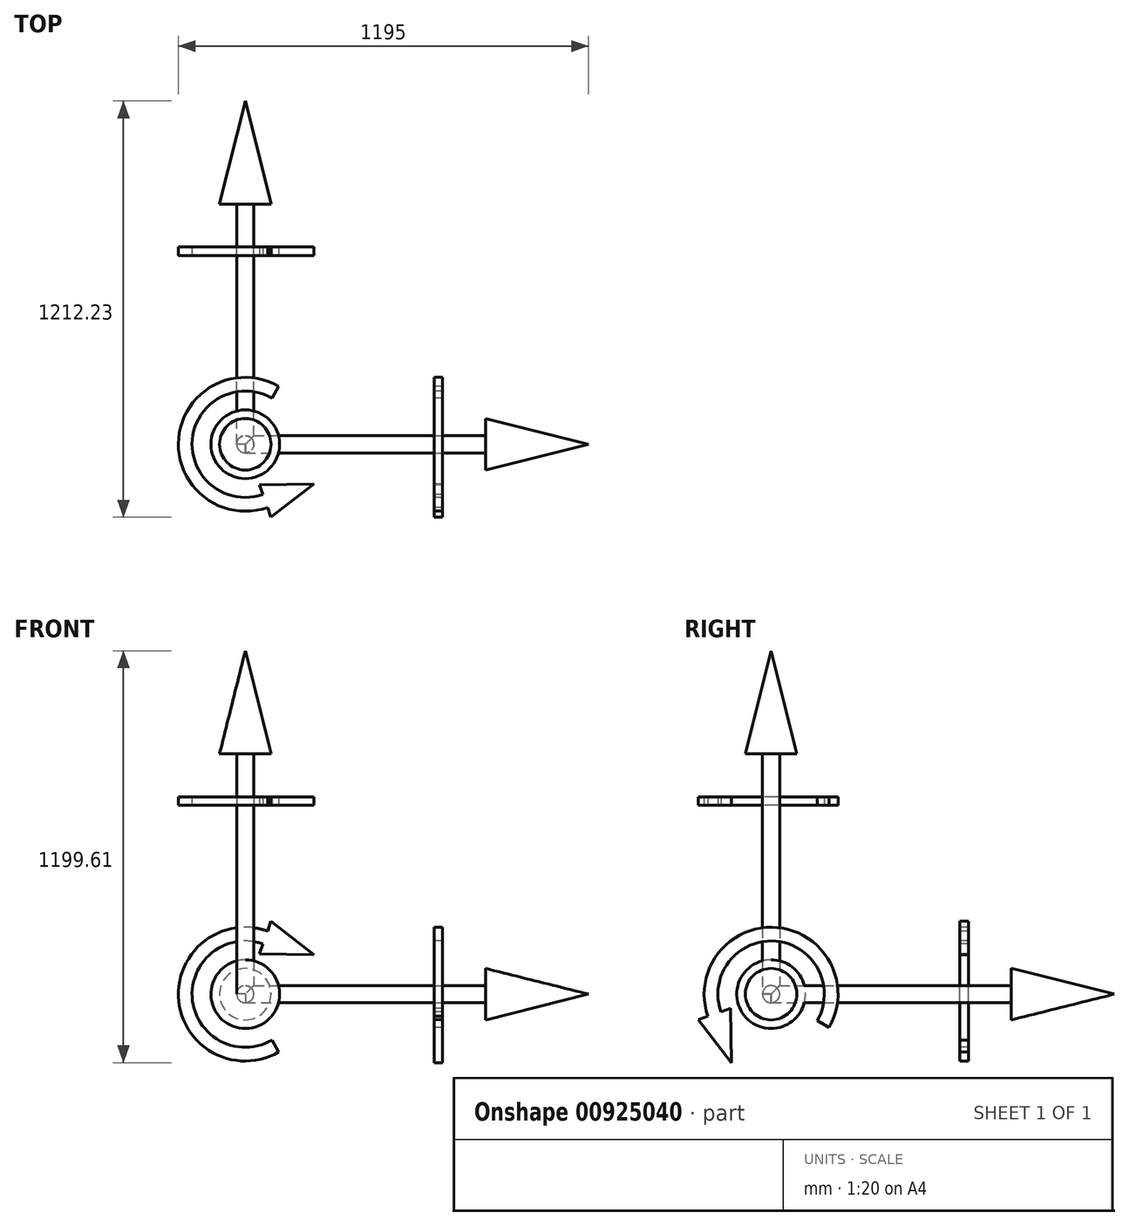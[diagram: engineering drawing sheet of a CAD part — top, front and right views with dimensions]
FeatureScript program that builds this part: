
annotation { "Feature Type Name" : "Feature", "Feature Type Description" : "" }
export const myFeature = defineFeature(function(context is Context, id is Id, definition is map)
    precondition{}
    {
        {
            var Q0;
            Q0=qCreatedBy(makeId("Front.planeOp"),FACE);
            var sketch = newSketch(context, id + "F0", { "sketchPlane" : qUnion([Q0])});
            skLineSegment(sketch, "E0.bottom", {"start": v(700, 0) * mm, "end": v(0, 0) * mm});
            skLineSegment(sketch, "E0.top", {"start": v(700, 25) * mm, "end": v(0, 25) * mm});
            skLineSegment(sketch, "E0.left", {"start": v(0, 0) * mm, "end": v(0, 25) * mm});
            skLineSegment(sketch, "E0.right", {"start": v(700, 0) * mm, "end": v(700, 25) * mm});
            skLineSegment(sketch, "E1", {"start": v(0, 0) * mm, "end": v(-428.97, 0) * mm, "construction": true});
            skLineSegment(sketch, "E2", {"start": v(700, 75) * mm, "end": v(1000, 0) * mm});
            skLineSegment(sketch, "E3", {"start": v(700, 0) * mm, "end": v(1000, 0) * mm});
            skLineSegment(sketch, "E4", {"start": v(700, 25) * mm, "end": v(700, 75) * mm});
            skSolve(sketch);
        }
        {
            var Q0;
            Q0=makeQuery(id+"F0.imprint","IMPRINT",FACE,{"disambiguationData":[TD([[makeQuery(id+"F0.imprint","IMPRINT",EDGE,{"derivedFrom":sQuery(id+"F0.wireOp",EDGE,"E0.right")}),-1.0]])]});
            var Q1;
            Q1=makeQuery(id+"F0.imprint","IMPRINT",FACE,{"disambiguationData":[TD([[makeQuery(id+"F0.imprint","IMPRINT",EDGE,{"derivedFrom":sQuery(id+"F0.wireOp",EDGE,"E0.bottom")}),-1.0]])]});
            var Q2;
            Q2=sQuery(id+"F0.wireOp",EDGE,"E0.bottom");
            revolve(context, id + "F1", {"surfaceOperationType" : NewSurfaceOperationType.NEW, "entities" : qUnion([Q0, Q1]), "axis" : qUnion([Q2]), "revolveType" : RevolveType.FULL});
        }
        {
            var Q0;
            Q0=qCreatedBy(makeId("Right.planeOp"),FACE);
            var sketch = newSketch(context, id + "F2", { "sketchPlane" : qUnion([Q0])});
            skLineSegment(sketch, "E5", {"start": v(1000, 0) * mm, "end": v(0, 0) * mm});
            skLineSegment(sketch, "E6", {"start": v(1000, 0) * mm, "end": v(700, 75) * mm});
            skLineSegment(sketch, "E7", {"start": v(700, 75) * mm, "end": v(700, 25) * mm});
            skLineSegment(sketch, "E8", {"start": v(0, 25) * mm, "end": v(700, 25) * mm});
            skLineSegment(sketch, "E9", {"start": v(0, 25) * mm, "end": v(0, 0) * mm});
            skSolve(sketch);
        }
        {
            var Q0;
            Q0=makeQuery(id+"F2.imprint","IMPRINT",FACE,{"disambiguationData":[TD([[makeQuery(id+"F2.imprint","IMPRINT",EDGE,{"derivedFrom":sQuery(id+"F2.wireOp",EDGE,"E5")}),-1.0]])]});
            var Q1;
            Q1=sQuery(id+"F2.wireOp",EDGE,"E5");
            revolve(context, id + "F3", {"operationType" : NewBodyOperationType.ADD, "surfaceOperationType" : NewSurfaceOperationType.NEW, "entities" : qUnion([Q0]), "axis" : qUnion([Q1]), "revolveType" : RevolveType.FULL});
        }
        {
            var Q0;
            Q0=qCreatedBy(makeId("Front.planeOp"),FACE);
            var sketch = newSketch(context, id + "F4", { "sketchPlane" : qUnion([Q0])});
            skLineSegment(sketch, "E10", {"start": v(0, 0) * mm, "end": v(0, 1000) * mm});
            skLineSegment(sketch, "E11", {"start": v(0, 1000) * mm, "end": v(-75, 700) * mm});
            skLineSegment(sketch, "E12", {"start": v(-75, 700) * mm, "end": v(-25, 700) * mm});
            skLineSegment(sketch, "E13", {"start": v(-25, 700) * mm, "end": v(-25, 0) * mm});
            skLineSegment(sketch, "E14", {"start": v(-25, 0) * mm, "end": v(0, 0) * mm});
            skSolve(sketch);
        }
        {
            var Q0;
            Q0=makeQuery(id+"F4.imprint","IMPRINT",FACE,{"disambiguationData":[TD([[makeQuery(id+"F4.imprint","IMPRINT",EDGE,{"derivedFrom":sQuery(id+"F4.wireOp",EDGE,"E10")}),1.0]])]});
            var Q1;
            Q1=sQuery(id+"F4.wireOp",EDGE,"E10");
            revolve(context, id + "F5", {"operationType" : NewBodyOperationType.ADD, "surfaceOperationType" : NewSurfaceOperationType.NEW, "entities" : qUnion([Q0]), "axis" : qUnion([Q1]), "revolveType" : RevolveType.FULL});
        }
        {
            var Q0;
            Q0=qCreatedBy(makeId("Right.planeOp"),FACE);
            var sketch = newSketch(context, id + "F6", { "sketchPlane" : qUnion([Q0])});
            skArc(sketch, "E15", {"start": v(0, -100) * mm, "mid": v(100, 0) * mm, "end": v(0, 100) * mm});
            skLineSegment(sketch, "E16", {"start": v(0, 100) * mm, "end": v(0, -100) * mm});
            skSolve(sketch);
        }
        {
            var Q0;
            Q0=makeQuery(id+"F6.imprint","IMPRINT",FACE,{"disambiguationData":[TD([[makeQuery(id+"F6.imprint","IMPRINT",EDGE,{"derivedFrom":sQuery(id+"F6.wireOp",EDGE,"E15")}),1.0]])]});
            var Q1;
            Q1=sQuery(id+"F6.wireOp",EDGE,"E16");
            revolve(context, id + "F7", {"surfaceOperationType" : NewSurfaceOperationType.NEW, "entities" : qUnion([Q0]), "axis" : qUnion([Q1]), "revolveType" : RevolveType.FULL});
        }
        {
            var Q0;
            Q0=qCreatedBy(makeId("Top.planeOp"),FACE);
            cPlane(context, id + "F8", {"entities" : qUnion([Q0]), "cplaneType" : CPlaneType.OFFSET, "offset" : 550 * mm, "width" : 150 * mm, "height" : 150 * mm});
        }
        {
            var Q0;
            Q0=qCreatedBy(id+"F8.planeOp",FACE);
            var sketch = newSketch(context, id + "F9", { "sketchPlane" : qUnion([Q0])});
            skArc(sketch, "E17", {"start": v(87.5, 151.55) * mm, "mid": v(-169.04, -45.3) * mm, "end": v(151.55, -87.5) * mm, "construction": true});
            skLineSegment(sketch, "E18", {"start": v(0, 0) * mm, "end": v(151.55, -87.5) * mm, "construction": true});
            skLineSegment(sketch, "E19", {"start": v(0, 0) * mm, "end": v(87.5, 151.55) * mm, "construction": true});
            skLineSegment(sketch, "E20", {"start": v(0, 0) * mm, "end": v(0, 998.9) * mm, "construction": true});
            skArc(sketch, "E21.0", {"start": v(97.5, 168.87) * mm, "mid": v(-194.17, 18.01) * mm, "end": v(64.77, -183.93) * mm});
            skArc(sketch, "E22.0", {"start": v(77.5, 134.23) * mm, "mid": v(-154.34, 14.32) * mm, "end": v(51.48, -146.2) * mm});
            skLineSegment(sketch, "E23", {"start": v(77.5, 134.23) * mm, "end": v(97.5, 168.87) * mm});
            skLineSegment(sketch, "E24", {"start": v(0, 0) * mm, "end": v(64.77, -183.93) * mm, "construction": true});
            skLineSegment(sketch, "E25", {"start": v(41.52, -117.9) * mm, "end": v(74.73, -212.23) * mm});
            skPoint(sketch, "E26", {"position": v(58.12, -165.07) * mm});
            skLineSegment(sketch, "E27", {"start": v(41.52, -117.9) * mm, "end": v(199.6, -115.24) * mm});
            skLineSegment(sketch, "E28", {"start": v(199.6, -115.24) * mm, "end": v(74.73, -212.23) * mm});
            skLineSegment(sketch, "E29", {"start": v(58.12, -165.07) * mm, "end": v(199.6, -115.24) * mm, "construction": true});
            skSolve(sketch);
        }
        {
            var Q0;
            {var subQ0=sQuery(id+"F9.wireOp",EDGE,"E21.0");Q0=makeQuery(id+"F9.imprint","IMPRINT",FACE,{"disambiguationData":[TD([[makeQuery(id+"F9.imprint","IMPRINT",EDGE,{"derivedFrom":subQ0}),1.0]])]});}
            var Q1;
            {var subQ0=sQuery(id+"F9.wireOp",EDGE,"E27");Q1=makeQuery(id+"F9.imprint","IMPRINT",FACE,{"disambiguationData":[TD([[makeQuery(id+"F9.imprint","IMPRINT",EDGE,{"derivedFrom":subQ0}),-1.0]])]});}
            extrude(context, id + "F10", {"entities" : qUnion([Q0, Q1]), "depth" : 25 * mm, "offsetDistance" : 25 * mm});
        }
        {
            var Q0;
            Q0=makeQuery(id+"F10.opExtrude","SWEPT_BODY",BODY,{"disambiguationData":[OSD([sQuery(id+"F9.wireOp",EDGE,"E21.0"),sQuery(id+"F9.wireOp",EDGE,"E22.0"),sQuery(id+"F9.wireOp",EDGE,"E23"),sQuery(id+"F9.wireOp",EDGE,"E25"),sQuery(id+"F9.wireOp",EDGE,"E27"),sQuery(id+"F9.wireOp",EDGE,"E28")])]});
            var Q1;
            Q1=makeQuery(id+"F3.opRevolve","SWEPT_FACE",FACE,{"disambiguationData":[OSD([sQuery(id+"F2.wireOp",EDGE,"E8")])]});
            transform(context, id + "F11", {"entities" : qUnion([Q0]), "transformType" : TransformType.ROTATION, "transformAxis" : qUnion([Q1]), "angle" : 90 * degree, "makeCopy" : true});
        }
        {
            var Q0;
            Q0=makeQuery(id+"F10.opExtrude","SWEPT_BODY",BODY,{"disambiguationData":[OSD([sQuery(id+"F9.wireOp",EDGE,"E21.0"),sQuery(id+"F9.wireOp",EDGE,"E22.0"),sQuery(id+"F9.wireOp",EDGE,"E23"),sQuery(id+"F9.wireOp",EDGE,"E25"),sQuery(id+"F9.wireOp",EDGE,"E27"),sQuery(id+"F9.wireOp",EDGE,"E28")])]});
            var Q1;
            Q1=makeQuery(id+"F1.opRevolve","SWEPT_FACE",FACE,{"disambiguationData":[OSD([sQuery(id+"F0.wireOp",EDGE,"E0.top")])]});
            transform(context, id + "F12", {"entities" : qUnion([Q0]), "transformType" : TransformType.ROTATION, "transformAxis" : qUnion([Q1]), "angle" : 90 * degree, "oppositeDirection" : true, "makeCopy" : true});
        }
    });
